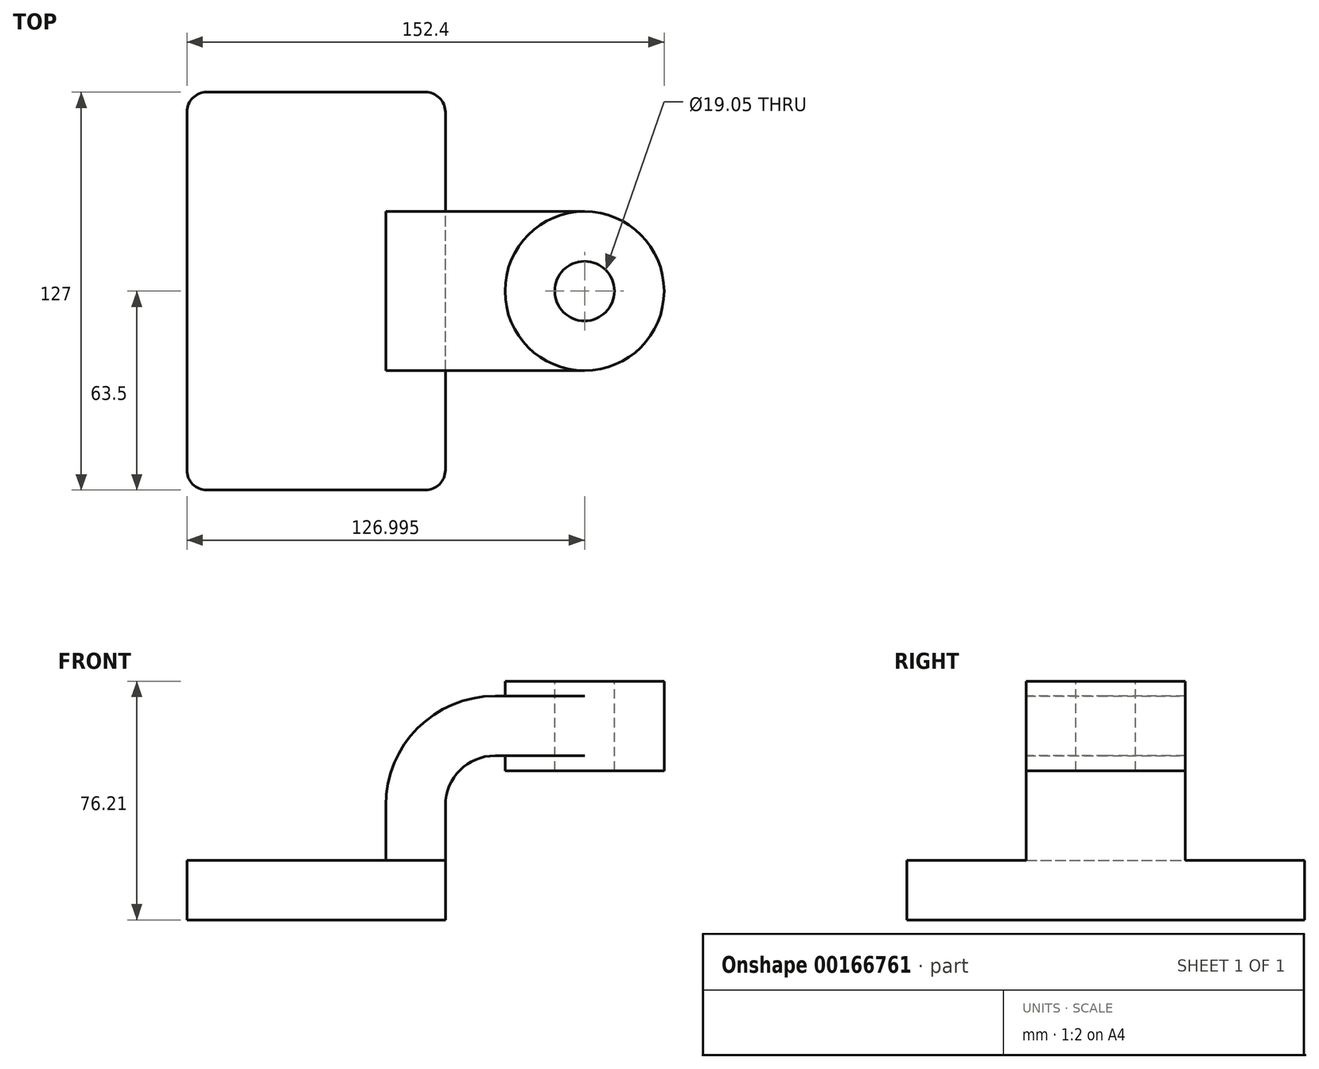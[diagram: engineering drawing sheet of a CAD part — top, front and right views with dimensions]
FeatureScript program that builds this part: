
annotation { "Feature Type Name" : "Feature", "Feature Type Description" : "" }
export const myFeature = defineFeature(function(context is Context, id is Id, definition is map)
    precondition{}
    {
        {
            var Q0;
            Q0=qCreatedBy(makeId("Front.planeOp"),FACE);
            var sketch = newSketch(context, id + "F0", { "sketchPlane" : qUnion([Q0])});
            skLineSegment(sketch, "E0.bottom", {"start": v(41.28, -9.52) * mm, "end": v(-41.28, -9.53) * mm});
            skLineSegment(sketch, "E0.top", {"start": v(41.28, 9.53) * mm, "end": v(-41.28, 9.53) * mm});
            skLineSegment(sketch, "E0.left", {"start": v(41.28, -9.52) * mm, "end": v(41.28, 9.53) * mm});
            skLineSegment(sketch, "E0.right", {"start": v(-41.28, -9.53) * mm, "end": v(-41.28, 9.53) * mm});
            skPoint(sketch, "E0.middle", {"position": v(0, 0) * mm});
            skLineSegment(sketch, "E1.bottom", {"start": v(111.12, 38.1) * mm, "end": v(60.32, 38.1) * mm});
            skLineSegment(sketch, "E1.top", {"start": v(111.13, 66.68) * mm, "end": v(60.33, 66.68) * mm});
            skLineSegment(sketch, "E1.left", {"start": v(111.13, 38.1) * mm, "end": v(111.13, 66.68) * mm});
            skLineSegment(sketch, "E1.right", {"start": v(60.33, 38.1) * mm, "end": v(60.33, 66.68) * mm});
            skPoint(sketch, "E1.middle", {"position": v(85.72, 52.39) * mm});
            skLineSegment(sketch, "E2", {"start": v(41.28, 9.53) * mm, "end": v(41.28, 27) * mm});
            skArc(sketch, "E3", {"start": v(41.27, 27) * mm, "mid": v(45.92, 38.23) * mm, "end": v(57.15, 42.88) * mm});
            skLineSegment(sketch, "E4", {"start": v(57.15, 42.88) * mm, "end": v(85.72, 42.88) * mm});
            skLineSegment(sketch, "E5.0", {"start": v(57.15, 61.93) * mm, "end": v(85.72, 61.93) * mm});
            skArc(sketch, "E5.1", {"start": v(22.23, 27) * mm, "mid": v(32.45, 51.7) * mm, "end": v(57.15, 61.93) * mm});
            skLineSegment(sketch, "E5.2", {"start": v(22.22, 9.53) * mm, "end": v(22.22, 27) * mm});
            skLineSegment(sketch, "E6", {"start": v(85.73, 38.1) * mm, "end": v(85.72, 42.88) * mm});
            skLineSegment(sketch, "E7", {"start": v(85.72, 42.88) * mm, "end": v(85.72, 52.39) * mm});
            skLineSegment(sketch, "E8", {"start": v(85.72, 52.39) * mm, "end": v(85.72, 61.93) * mm});
            skLineSegment(sketch, "E9", {"start": v(85.72, 61.93) * mm, "end": v(85.73, 66.68) * mm});
            skFitSpline(sketch, "E10", {"points": [v(-41.28, 9.52) * mm, v(57.15, 61.93) * mm], "startDerivative": vector(-0.56, 73.31) * mm, "endDerivative": vector(122.83, -1) * mm});
            skSolve(sketch);
        }
        {
            var Q0;
            Q0=makeQuery(id+"F0.imprint","IMPRINT",FACE,{"disambiguationData":[TD([[makeQuery(id+"F0.imprint","IMPRINT",EDGE,{"derivedFrom":sQuery(id+"F0.wireOp",EDGE,"E0.bottom")}),-1.0]])]});
            extrude(context, id + "F1", {"entities" : qUnion([Q0]), "endBound" : BoundingType.SYMMETRIC, "depth" : 127 * mm});
        }
        {
            var Q0;
            {var subQ1=sQuery(id+"F0.wireOp",EDGE,"E2");Q0=makeQuery(id+"F0.imprint","IMPRINT",FACE,{"disambiguationData":[TD([[makeQuery(id+"F0.imprint","IMPRINT",EDGE,{"derivedFrom":subQ1}),1.0]])]});}
            var Q1;
            {var subQ0=sQuery(id+"F0.wireOp",EDGE,"E7");Q1=makeQuery(id+"F0.imprint","IMPRINT",FACE,{"disambiguationData":[TD([[makeQuery(id+"F0.imprint","IMPRINT",EDGE,{"derivedFrom":subQ0}),1.0]])]});}
            extrude(context, id + "F2", {"entities" : qUnion([Q0, Q1]), "operationType" : NewBodyOperationType.ADD, "endBound" : BoundingType.SYMMETRIC, "depth" : 50.8 * mm});
        }
        {
            var Q0;
            Q0=makeQuery(id+"F0.imprint","IMPRINT",FACE,{"disambiguationData":[TD([[makeQuery(id+"F0.imprint","IMPRINT",EDGE,{"derivedFrom":sQuery(id+"F0.wireOp",EDGE,"E5.1")}),1.0]])]});
            extrude(context, id + "F3", {"entities" : qUnion([Q0]), "operationType" : NewBodyOperationType.ADD, "endBound" : BoundingType.SYMMETRIC, "depth" : 15.88 * mm});
        }
        {
            var Q0;
            {var subQ0=sQuery(id+"F0.wireOp",EDGE,"E1.left");Q0=makeQuery(id+"F0.imprint","IMPRINT",FACE,{"disambiguationData":[TD([[makeQuery(id+"F0.imprint","IMPRINT",EDGE,{"derivedFrom":subQ0}),1.0]])]});}
            var Q1;
            Q1=sQuery(id+"F0.wireOp",EDGE,"E8");
            revolve(context, id + "F4", {"operationType" : NewBodyOperationType.ADD, "entities" : qUnion([Q0]), "axis" : qUnion([Q1]), "revolveType" : RevolveType.FULL});
        }
        {
            var Q0;
            Q0=makeQuery(id+"F1.opExtrude","CAP_EDGE",EDGE,{"disambiguationData":[OSD([sQuery(id+"F0.wireOp",EDGE,"E0.left")])],"isStart":false});
            var Q1;
            Q1=makeQuery(id+"F1.opExtrude","CAP_EDGE",EDGE,{"disambiguationData":[OSD([sQuery(id+"F0.wireOp",EDGE,"E0.right")])],"isStart":false});
            var Q2;
            Q2=makeQuery(id+"F1.opExtrude","CAP_EDGE",EDGE,{"disambiguationData":[OSD([sQuery(id+"F0.wireOp",EDGE,"E0.left")])],"isStart":true});
            var Q3;
            Q3=makeQuery(id+"F1.opExtrude","CAP_EDGE",EDGE,{"disambiguationData":[OSD([sQuery(id+"F0.wireOp",EDGE,"E0.right")])],"isStart":true});
            fillet(context, id + "F5", {"entities" : qUnion([Q0, Q1, Q2, Q3]), "radius" : 6.35 * mm, "tangentPropagation" : true, "allowEdgeOverflow" : false});
        }
        {
            var Q0;
            Q0=makeQuery(id+"F4.opRevolve","SWEPT_FACE",FACE,{"disambiguationData":[OSD([sQuery(id+"F0.wireOp",EDGE,"E1.top")])]});
            var sketch = newSketch(context, id + "F6", { "sketchPlane" : qUnion([Q0])});
            skPoint(sketch, "E11", {"position": v(85.72, 0) * mm});
            skSolve(sketch);
        }
        {
            var Q0;
            Q0=sQuery(id+"F6.wireOp",VERTEX,"E11");
            var Q1;
            Q1=makeQuery(id+"F1.opExtrude","SWEPT_BODY",BODY,{"disambiguationData":[OSD([sQuery(id+"F0.wireOp",EDGE,"E0.bottom"),sQuery(id+"F0.wireOp",EDGE,"E0.top"),sQuery(id+"F0.wireOp",EDGE,"E0.left"),sQuery(id+"F0.wireOp",EDGE,"E0.right")])]});
            hole(context, id + "F7", {"style" : HoleStyle.SIMPLE, "endStyle" : HoleEndStyle.THROUGH, "holeDiameter" : 19.05 * mm, "locations" : qUnion([Q0]), "scope" : qUnion([Q1]), "isTappedThrough" : true});
        }
    });
